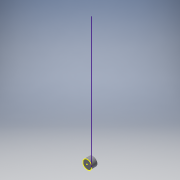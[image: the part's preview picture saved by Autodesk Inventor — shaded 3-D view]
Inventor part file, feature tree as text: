
AUTODESK INVENTOR PART (.ipt)
format: ipt  version: 2016 (Build 200138000, 138)  size: 99,840 bytes
history: native  units: in
note: dims shown in document units (in); Inventor stores cm internally (conversion verified against a paired STEP export)
features: sketch x3, extrude x2, reference x1
ambient origin geometry x8: Origin, YZ Plane, XZ Plane, XY Plane, X Axis, Y Axis, Z Axis, Center Point
bodies: Solid1 (feature_tree)
feature tree (6):
  extrude  "Extrusion1"  Depth=0.3937in
  extrude  "Extrusion2"  [1 undecoded]
  sketch  "Sketch3"
  sketch  "Sketch1"  dims[d0=0.601in d1=0.0in d2=0.3937in]
  reference  "Reference1"
  sketch  "Sketch2"  dims[d3=0.3937in d4=0.0in]
note: 1 required parameter value undecoded (feature->parameter linkage not recoverable at this tier; creation-order binding heuristic only, values carry confidence <= 0.55)
